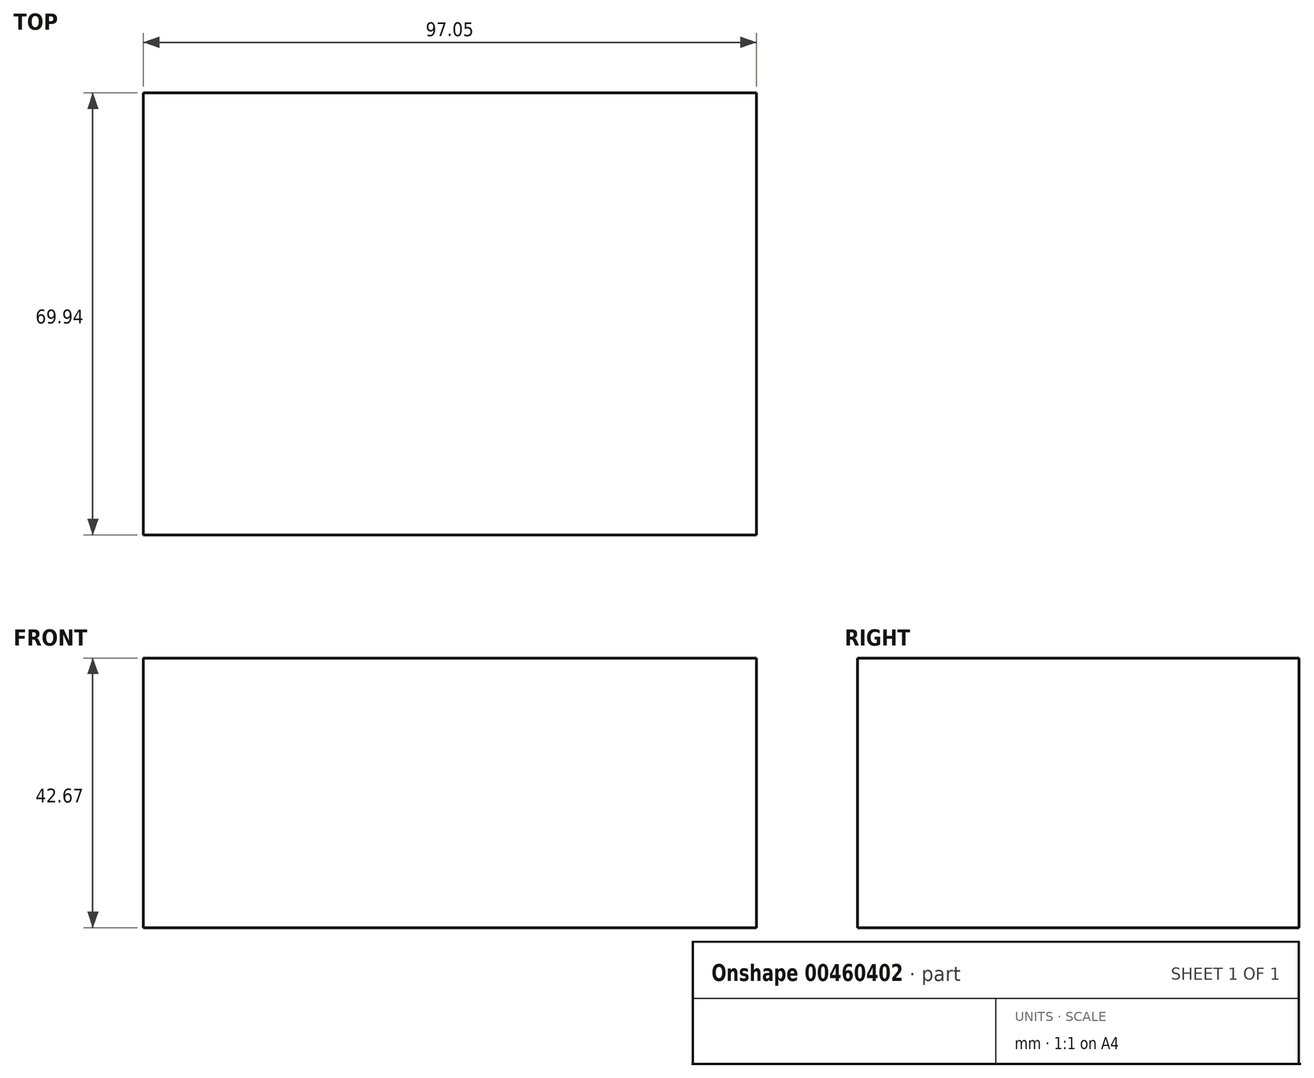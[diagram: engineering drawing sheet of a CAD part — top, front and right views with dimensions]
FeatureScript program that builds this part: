
annotation { "Feature Type Name" : "Feature", "Feature Type Description" : "" }
export const myFeature = defineFeature(function(context is Context, id is Id, definition is map)
    precondition{}
    {
        {
            var Q0;
            Q0=qCreatedBy(makeId("Top.planeOp"),FACE);
            var sketch = newSketch(context, id + "F0", { "sketchPlane" : qUnion([Q0])});
            skLineSegment(sketch, "E0.bottom", {"start": v(-111.2, -62.94) * mm, "end": v(-14.15, -62.94) * mm});
            skLineSegment(sketch, "E0.top", {"start": v(-111.2, 7) * mm, "end": v(-14.15, 7) * mm});
            skLineSegment(sketch, "E0.left", {"start": v(-111.2, -62.94) * mm, "end": v(-111.2, 7) * mm});
            skLineSegment(sketch, "E0.right", {"start": v(-14.15, -62.94) * mm, "end": v(-14.15, 7) * mm});
            skSolve(sketch);
        }
        {
            var Q0;
            Q0=makeQuery(id+"F0.imprint","IMPRINT",FACE,{"disambiguationData":[TD([[makeQuery(id+"F0.imprint","IMPRINT",EDGE,{"derivedFrom":sQuery(id+"F0.wireOp",EDGE,"E0.bottom")}),1.0]])]});
            extrude(context, id + "F1", {"entities" : qUnion([Q0]), "depth" : 42.67 * mm});
        }
    });
